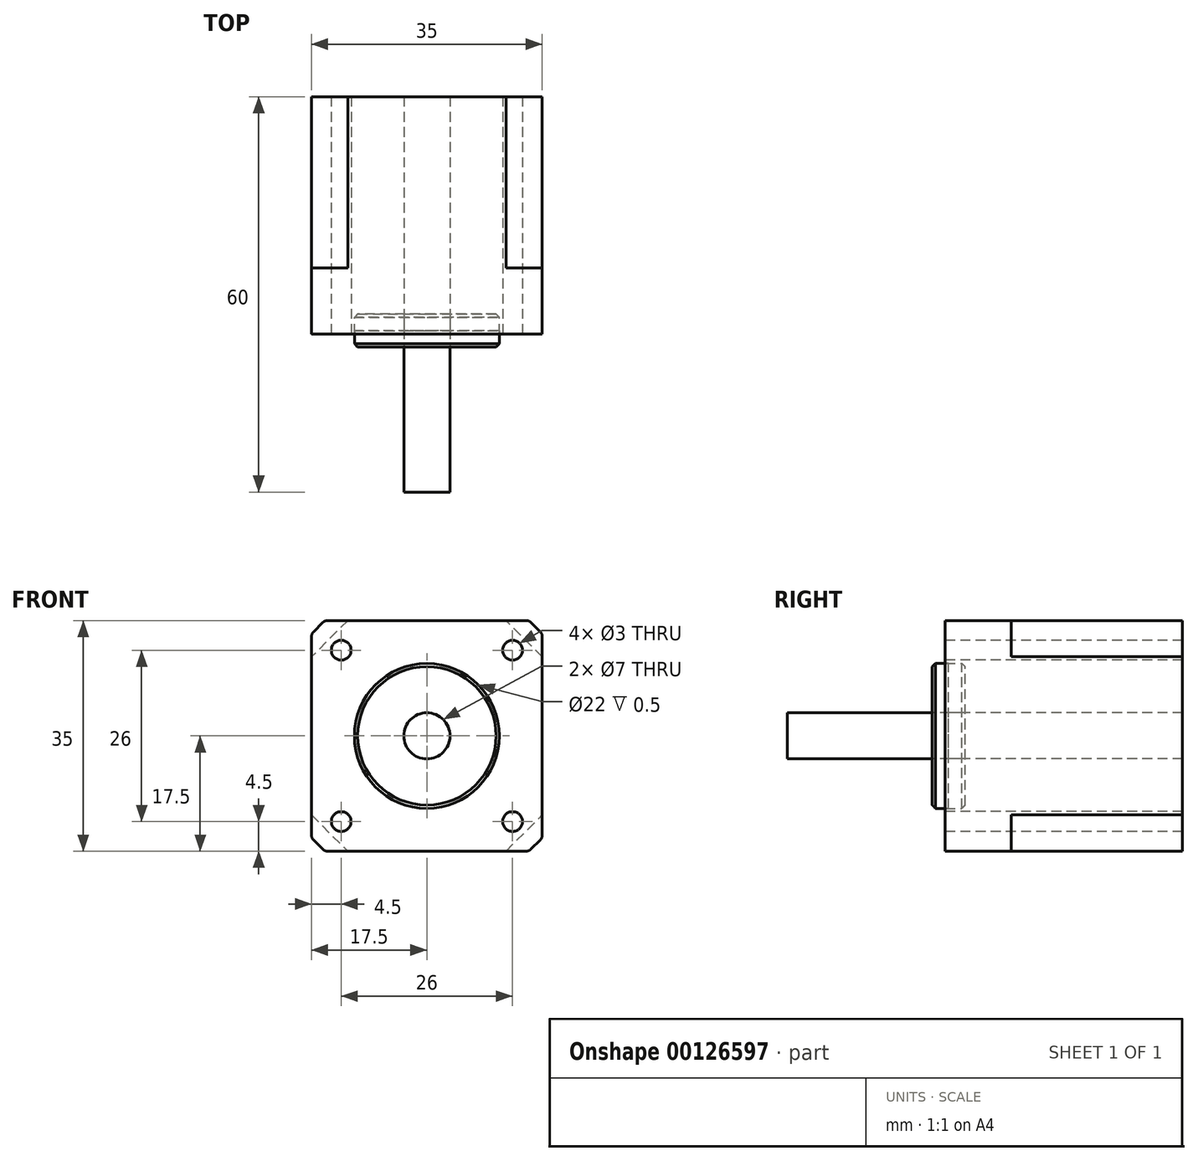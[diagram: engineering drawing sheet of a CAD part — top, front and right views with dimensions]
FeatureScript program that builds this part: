
annotation { "Feature Type Name" : "Feature", "Feature Type Description" : "" }
export const myFeature = defineFeature(function(context is Context, id is Id, definition is map)
    precondition{}
    {
        {
            var Q0;
            Q0=qCreatedBy(makeId("Front.planeOp"),FACE);
            var sketch = newSketch(context, id + "F0", { "sketchPlane" : qUnion([Q0])});
            skLineSegment(sketch, "E0.bottom", {"start": v(-17.5, 17.5) * mm, "end": v(17.5, 17.5) * mm});
            skLineSegment(sketch, "E0.top", {"start": v(-17.5, -17.5) * mm, "end": v(17.5, -17.5) * mm});
            skLineSegment(sketch, "E0.left", {"start": v(-17.5, 17.5) * mm, "end": v(-17.5, -17.5) * mm});
            skLineSegment(sketch, "E0.right", {"start": v(17.5, 17.5) * mm, "end": v(17.5, -17.5) * mm});
            skPoint(sketch, "E0.middle", {"position": v(0, 0) * mm});
            skSolve(sketch);
        }
        {
            var Q0;
            Q0=makeQuery(id+"F0.imprint","IMPRINT",FACE,{"disambiguationData":[TD([[makeQuery(id+"F0.imprint","IMPRINT",EDGE,{"derivedFrom":sQuery(id+"F0.wireOp",EDGE,"E0.bottom")}),-1.0]])]});
            extrude(context, id + "F1", {"entities" : qUnion([Q0]), "depth" : 10 * mm, "offsetDistance" : 25 * mm});
        }
        {
            var Q0;
            Q0=makeQuery(id+"F1.opExtrude","SWEPT_EDGE",EDGE,{"disambiguationData":[OSD([sQuery(id+"F0.wireOp",EDGE,"E0.bottom"),sQuery(id+"F0.wireOp",EDGE,"E0.left")])]});
            var Q1;
            Q1=makeQuery(id+"F1.opExtrude","SWEPT_EDGE",EDGE,{"disambiguationData":[OSD([sQuery(id+"F0.wireOp",EDGE,"E0.bottom"),sQuery(id+"F0.wireOp",EDGE,"E0.right")])]});
            var Q2;
            Q2=makeQuery(id+"F1.opExtrude","SWEPT_EDGE",EDGE,{"disambiguationData":[OSD([sQuery(id+"F0.wireOp",EDGE,"E0.top"),sQuery(id+"F0.wireOp",EDGE,"E0.right")])]});
            var Q3;
            Q3=makeQuery(id+"F1.opExtrude","SWEPT_EDGE",EDGE,{"disambiguationData":[OSD([sQuery(id+"F0.wireOp",EDGE,"E0.top"),sQuery(id+"F0.wireOp",EDGE,"E0.left")])]});
            chamfer(context, id + "F2", {"entities" : qUnion([Q0, Q1, Q2, Q3]), "width" : 2 * mm, "tangentPropagation" : true});
        }
        {
            var Q0;
            Q0=makeQuery(id+"F1.opExtrude","CAP_FACE",FACE,{"disambiguationData":[OSD([sQuery(id+"F0.wireOp",EDGE,"E0.bottom"),sQuery(id+"F0.wireOp",EDGE,"E0.top"),sQuery(id+"F0.wireOp",EDGE,"E0.left"),sQuery(id+"F0.wireOp",EDGE,"E0.right")])],"isStart":false});
            var sketch = newSketch(context, id + "F3", { "sketchPlane" : qUnion([Q0])});
            skCircle(sketch, "E1", {"center": v(0, 0) * mm, "radius": 11 * mm});
            skSolve(sketch);
        }
        {
            var Q0;
            Q0=makeQuery(id+"F3.imprint","IMPRINT",FACE,{"disambiguationData":[TD([[makeQuery(id+"F3.imprint","IMPRINT",EDGE,{"derivedFrom":sQuery(id+"F3.wireOp",EDGE,"E1")}),1.0]])]});
            extrude(context, id + "F4", {"entities" : qUnion([Q0]), "operationType" : NewBodyOperationType.REMOVE, "oppositeDirection" : true, "depth" : 0.5 * mm, "offsetDistance" : 25 * mm});
        }
        {
            var Q0;
            Q0=makeQuery(id+"F4.boolean.opBoolean","COPY",FACE,{"derivedFrom":makeQuery(id+"F4.opExtrude","CAP_FACE",FACE,{"disambiguationData":[OSD([sQuery(id+"F3.wireOp",EDGE,"E1")])],"isStart":false})});
            var sketch = newSketch(context, id + "F5", { "sketchPlane" : qUnion([Q0])});
            skCircle(sketch, "E2", {"center": v(0, 0) * mm, "radius": 11 * mm});
            skSolve(sketch);
        }
        {
            var Q0;
            Q0=makeQuery(id+"F5.imprint","IMPRINT",FACE,{"disambiguationData":[TD([[makeQuery(id+"F5.imprint","IMPRINT",EDGE,{"derivedFrom":sQuery(id+"F5.wireOp",EDGE,"E2")}),1.0]])]});
            extrude(context, id + "F6", {"entities" : qUnion([Q0]), "depth" : 5 * mm, "offsetDistance" : 25 * mm, "symmetric" : true});
        }
        {
            var Q0;
            Q0=makeQuery(id+"F6.opExtrude","CAP_FACE",FACE,{"disambiguationData":[OSD([sQuery(id+"F5.wireOp",EDGE,"E2")])],"isStart":false});
            var sketch = newSketch(context, id + "F7", { "sketchPlane" : qUnion([Q0])});
            skCircle(sketch, "E3", {"center": v(0, 0) * mm, "radius": 3.5 * mm});
            skSolve(sketch);
        }
        {
            var Q0;
            Q0=makeQuery(id+"F7.imprint","IMPRINT",FACE,{"disambiguationData":[TD([[makeQuery(id+"F7.imprint","IMPRINT",EDGE,{"derivedFrom":sQuery(id+"F7.wireOp",EDGE,"E3")}),1.0]])]});
            var Q1;
            Q1=sQuery(id+"F7.wireOp",EDGE,"E3");
            extrude(context, id + "F8", {"entities" : qUnion([Q0]), "operationType" : NewBodyOperationType.REMOVE, "surfaceEntities" : qUnion([Q1]), "endBound" : BoundingType.THROUGH_ALL, "oppositeDirection" : true, "depth" : 25 * mm, "offsetDistance" : 25 * mm});
        }
        {
            var Q0;
            {var subQ0=sQuery(id+"F0.wireOp",EDGE,"E0.bottom");Q0=makeQuery(id+"F2.opChamfer","BLEND_EDGE",EDGE,{"blendedFrom":[makeQuery(id+"F1.opExtrude","SWEPT_EDGE",EDGE,{"disambiguationData":[OSD([subQ0,sQuery(id+"F0.wireOp",EDGE,"E0.left")])]}),makeQuery(id+"F1.opExtrude","SWEPT_FACE",FACE,{"disambiguationData":[OSD([subQ0])]})],"blendedInto":[makeQuery(id+"F1.opExtrude","SWEPT_FACE",FACE,{"disambiguationData":[OSD([subQ0])]})]});}
            var Q1;
            {var subQ0=sQuery(id+"F0.wireOp",EDGE,"E0.bottom");Q1=makeQuery(id+"F2.opChamfer","BLEND_EDGE",EDGE,{"blendedFrom":[makeQuery(id+"F1.opExtrude","SWEPT_EDGE",EDGE,{"disambiguationData":[OSD([subQ0,sQuery(id+"F0.wireOp",EDGE,"E0.right")])]}),makeQuery(id+"F1.opExtrude","SWEPT_FACE",FACE,{"disambiguationData":[OSD([subQ0])]})],"blendedInto":[makeQuery(id+"F1.opExtrude","SWEPT_FACE",FACE,{"disambiguationData":[OSD([subQ0])]})]});}
            var Q2;
            {var subQ0=sQuery(id+"F0.wireOp",EDGE,"E0.right");Q2=makeQuery(id+"F2.opChamfer","BLEND_EDGE",EDGE,{"blendedFrom":[makeQuery(id+"F1.opExtrude","SWEPT_EDGE",EDGE,{"disambiguationData":[OSD([sQuery(id+"F0.wireOp",EDGE,"E0.bottom"),subQ0])]}),makeQuery(id+"F1.opExtrude","SWEPT_FACE",FACE,{"disambiguationData":[OSD([subQ0])]})],"blendedInto":[makeQuery(id+"F1.opExtrude","SWEPT_FACE",FACE,{"disambiguationData":[OSD([subQ0])]})]});}
            var Q3;
            {var subQ0=sQuery(id+"F0.wireOp",EDGE,"E0.right");Q3=makeQuery(id+"F2.opChamfer","BLEND_EDGE",EDGE,{"blendedFrom":[makeQuery(id+"F1.opExtrude","SWEPT_EDGE",EDGE,{"disambiguationData":[OSD([sQuery(id+"F0.wireOp",EDGE,"E0.top"),subQ0])]}),makeQuery(id+"F1.opExtrude","SWEPT_FACE",FACE,{"disambiguationData":[OSD([subQ0])]})],"blendedInto":[makeQuery(id+"F1.opExtrude","SWEPT_FACE",FACE,{"disambiguationData":[OSD([subQ0])]})]});}
            var Q4;
            {var subQ0=sQuery(id+"F0.wireOp",EDGE,"E0.top");Q4=makeQuery(id+"F2.opChamfer","BLEND_EDGE",EDGE,{"blendedFrom":[makeQuery(id+"F1.opExtrude","SWEPT_EDGE",EDGE,{"disambiguationData":[OSD([subQ0,sQuery(id+"F0.wireOp",EDGE,"E0.right")])]}),makeQuery(id+"F1.opExtrude","SWEPT_FACE",FACE,{"disambiguationData":[OSD([subQ0])]})],"blendedInto":[makeQuery(id+"F1.opExtrude","SWEPT_FACE",FACE,{"disambiguationData":[OSD([subQ0])]})]});}
            var Q5;
            {var subQ0=sQuery(id+"F0.wireOp",EDGE,"E0.top");Q5=makeQuery(id+"F2.opChamfer","BLEND_EDGE",EDGE,{"blendedFrom":[makeQuery(id+"F1.opExtrude","SWEPT_EDGE",EDGE,{"disambiguationData":[OSD([subQ0,sQuery(id+"F0.wireOp",EDGE,"E0.left")])]}),makeQuery(id+"F1.opExtrude","SWEPT_FACE",FACE,{"disambiguationData":[OSD([subQ0])]})],"blendedInto":[makeQuery(id+"F1.opExtrude","SWEPT_FACE",FACE,{"disambiguationData":[OSD([subQ0])]})]});}
            var Q6;
            {var subQ0=sQuery(id+"F0.wireOp",EDGE,"E0.left");Q6=makeQuery(id+"F2.opChamfer","BLEND_EDGE",EDGE,{"blendedFrom":[makeQuery(id+"F1.opExtrude","SWEPT_EDGE",EDGE,{"disambiguationData":[OSD([sQuery(id+"F0.wireOp",EDGE,"E0.top"),subQ0])]}),makeQuery(id+"F1.opExtrude","SWEPT_FACE",FACE,{"disambiguationData":[OSD([subQ0])]})],"blendedInto":[makeQuery(id+"F1.opExtrude","SWEPT_FACE",FACE,{"disambiguationData":[OSD([subQ0])]})]});}
            var Q7;
            {var subQ0=sQuery(id+"F0.wireOp",EDGE,"E0.left");Q7=makeQuery(id+"F2.opChamfer","BLEND_EDGE",EDGE,{"blendedFrom":[makeQuery(id+"F1.opExtrude","SWEPT_EDGE",EDGE,{"disambiguationData":[OSD([sQuery(id+"F0.wireOp",EDGE,"E0.bottom"),subQ0])]}),makeQuery(id+"F1.opExtrude","SWEPT_FACE",FACE,{"disambiguationData":[OSD([subQ0])]})],"blendedInto":[makeQuery(id+"F1.opExtrude","SWEPT_FACE",FACE,{"disambiguationData":[OSD([subQ0])]})]});}
            fillet(context, id + "F9", {"entities" : qUnion([Q0, Q1, Q2, Q3, Q4, Q5, Q6, Q7]), "radius" : 1 * mm, "tangentPropagation" : true, "allowEdgeOverflow" : false});
        }
        {
            var Q0;
            Q0=makeQuery(id+"F6.opExtrude","CAP_EDGE",EDGE,{"disambiguationData":[OSD([sQuery(id+"F5.wireOp",EDGE,"E2")])],"isStart":false});
            var Q1;
            Q1=makeQuery(id+"F8.boolean.opBoolean","COPY",EDGE,{"derivedFrom":makeQuery(id+"F8.opExtrude","CAP_EDGE",EDGE,{"disambiguationData":[OSD([sQuery(id+"F7.wireOp",EDGE,"E3")])],"isStart":true})});
            var Q2;
            Q2=makeQuery(id+"F6.opExtrude","CAP_EDGE",EDGE,{"disambiguationData":[OSD([sQuery(id+"F5.wireOp",EDGE,"E2")])],"isStart":true});
            chamfer(context, id + "F10", {"entities" : qUnion([Q0, Q1, Q2]), "width" : 0.5 * mm, "tangentPropagation" : true});
        }
        {
            var Q0;
            Q0=makeQuery(id+"F1.opExtrude","CAP_FACE",FACE,{"disambiguationData":[OSD([sQuery(id+"F0.wireOp",EDGE,"E0.bottom"),sQuery(id+"F0.wireOp",EDGE,"E0.top"),sQuery(id+"F0.wireOp",EDGE,"E0.left"),sQuery(id+"F0.wireOp",EDGE,"E0.right")])],"isStart":false});
            var sketch = newSketch(context, id + "F11", { "sketchPlane" : qUnion([Q0])});
            skCircle(sketch, "E4", {"center": v(-13, 13) * mm, "radius": 1.5 * mm});
            skCircle(sketch, "E5.1.0", {"center": v(-13, -13) * mm, "radius": 1.5 * mm});
            skCircle(sketch, "E5.2.0", {"center": v(13, -13) * mm, "radius": 1.5 * mm});
            skCircle(sketch, "E5.3.0", {"center": v(13, 13) * mm, "radius": 1.5 * mm});
            skPoint(sketch, "E5.center", {"position": v(0, 0) * mm});
            skSolve(sketch);
        }
        {
            var Q0;
            Q0=qSketchRegion(id+"F11",true);
            extrude(context, id + "F12", {"entities" : qUnion([Q0]), "operationType" : NewBodyOperationType.REMOVE, "endBound" : BoundingType.THROUGH_ALL, "oppositeDirection" : true, "depth" : 25 * mm, "offsetDistance" : 25 * mm});
        }
        {
            var Q0;
            Q0=makeQuery(id+"F1.opExtrude","CAP_FACE",FACE,{"disambiguationData":[OSD([sQuery(id+"F0.wireOp",EDGE,"E0.bottom"),sQuery(id+"F0.wireOp",EDGE,"E0.top"),sQuery(id+"F0.wireOp",EDGE,"E0.left"),sQuery(id+"F0.wireOp",EDGE,"E0.right")])],"isStart":true});
            var sketch = newSketch(context, id + "F13", { "sketchPlane" : qUnion([Q0])});
            skLineSegment(sketch, "E6.bottom", {"start": v(-12, 17.5) * mm, "end": v(12, 17.5) * mm});
            skLineSegment(sketch, "E6.top", {"start": v(-12, -17.5) * mm, "end": v(12, -17.5) * mm});
            skLineSegment(sketch, "E6.left", {"start": v(-17.5, 12) * mm, "end": v(-17.5, -12) * mm});
            skLineSegment(sketch, "E6.right", {"start": v(17.5, 12) * mm, "end": v(17.5, -12) * mm});
            skPoint(sketch, "E6.middle", {"position": v(0, 0) * mm});
            skLineSegment(sketch, "E7", {"start": v(-17.5, 12) * mm, "end": v(-12, 17.5) * mm});
            skLineSegment(sketch, "E8.1.0", {"start": v(-12, -17.5) * mm, "end": v(-17.5, -12) * mm});
            skLineSegment(sketch, "E8.2.0", {"start": v(17.5, -12) * mm, "end": v(12, -17.5) * mm});
            skLineSegment(sketch, "E8.3.0", {"start": v(12, 17.5) * mm, "end": v(17.5, 12) * mm});
            skPoint(sketch, "E9.orphan", {"position": v(-17.5, 17.5) * mm});
            skPoint(sketch, "E10.orphan", {"position": v(-17.5, -17.5) * mm});
            skPoint(sketch, "E11.orphan", {"position": v(17.5, -17.5) * mm});
            skPoint(sketch, "E12.orphan", {"position": v(17.5, 17.5) * mm});
            skSolve(sketch);
        }
        {
            var Q0;
            Q0=qSketchRegion(id+"F13",true);
            extrude(context, id + "F14", {"entities" : qUnion([Q0]), "operationType" : NewBodyOperationType.REMOVE, "oppositeDirection" : true, "depth" : 4 * mm, "offsetDistance" : 25 * mm});
        }
        {
            var Q0;
            Q0=makeQuery(id+"F14.boolean.opBoolean","COPY",FACE,{"derivedFrom":makeQuery(id+"F14.opExtrude","CAP_FACE",FACE,{"disambiguationData":[OSD([sQuery(id+"F13.wireOp",EDGE,"E6.bottom"),sQuery(id+"F13.wireOp",EDGE,"E6.top"),sQuery(id+"F13.wireOp",EDGE,"E6.left"),sQuery(id+"F13.wireOp",EDGE,"E6.right"),sQuery(id+"F13.wireOp",EDGE,"E7"),sQuery(id+"F13.wireOp",EDGE,"E8.1.0"),sQuery(id+"F13.wireOp",EDGE,"E8.2.0"),sQuery(id+"F13.wireOp",EDGE,"E8.3.0")])],"isStart":false})});
            extrude(context, id + "F15", {"entities" : qUnion([Q0]), "operationType" : NewBodyOperationType.ADD, "depth" : 30 * mm, "offsetDistance" : 25 * mm});
        }
        {
            var Q0;
            Q0=makeQuery(id+"F1.opExtrude","CAP_FACE",FACE,{"disambiguationData":[OSD([sQuery(id+"F0.wireOp",EDGE,"E0.bottom"),sQuery(id+"F0.wireOp",EDGE,"E0.top"),sQuery(id+"F0.wireOp",EDGE,"E0.left"),sQuery(id+"F0.wireOp",EDGE,"E0.right")])],"isStart":false});
            cPlane(context, id + "F16", {"entities" : qUnion([Q0]), "cplaneType" : CPlaneType.OFFSET, "offset" : (42 / 2) * mm, "oppositeDirection" : true, "width" : 150 * mm, "height" : 150 * mm});
        }
        {
            var Q0;
            Q0=makeQuery(id+"F7.imprint","IMPRINT",FACE,{"disambiguationData":[TD([[makeQuery(id+"F7.imprint","IMPRINT",EDGE,{"derivedFrom":sQuery(id+"F7.wireOp",EDGE,"E3")}),1.0]])]});
            extrude(context, id + "F17", {"entities" : qUnion([Q0]), "operationType" : NewBodyOperationType.ADD, "depth" : 22 * mm, "offsetDistance" : 25 * mm});
        }
    });
